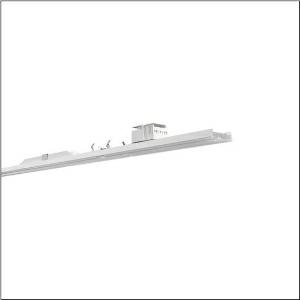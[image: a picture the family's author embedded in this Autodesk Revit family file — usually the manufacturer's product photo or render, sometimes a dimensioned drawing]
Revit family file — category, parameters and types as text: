
# Revit family: licross_r__11_recessed_mo_51tl18cn48xf_f7f9
name_source: partatom
category: Lighting Fixtures
units: mm (PartAtom-declared; Revit-internal decimal feet)

## family parameters
Cut with Voids When Loaded = No
Host = Face
Light Source = No
Part Type = Normal
Room Calculation Point = No
Round Connector Dimension = Use Diameter
Shared = No

## types (1)
- --- (1 x LED, 8060 lm, 48 W, 4000K)
    Apparent Load = 48 VA
    CIE Flux Codes = 83 96 99 100 100
    Color Rendering = 80
    Color Temperature = 4000K
    Default Elevation = 1800 mm
    Description = Licross® 11 Recessed MOluminaire insert, length: 1.500mm, width: 66mm, height: 67mm, LED rated luminous flux: 8.060lm, light colour: 840, control gear: ON/OFF Multilumen, CLOi, control gear: ECG Multilumen, with plug, 3-pole, with phase selection, mains connection: 220..240V, AC, 50/60Hz, halogen-free wiring, primary optical cover: cover, of PMMA, light emission: direct distribution, protection rating (complete): IP40, insulation class (complete): insulation class I (protective earthing), certification: CE, ENEC, VDE, protection symbol: D if used in an environment without relevant dust loads with corresponding accessories, permissible ambient temperature for indoor applications: -35..+40°C, reducing of maximum allowable ambient temperature of 5°C with ceiling mounting, corresponds to IFS (International Featured Standards) requirements for safety and quality in the food industry, packaging unit: 1 piece
    Height = 58 mm
    Lamp = 1 x LED
    Lamp Light Flux = 8060 lm
    Lamp Power = 48 W
    Lamp count = 1
    Length = 1500 mm
    Luminous efficacy = 168 lm/W
    Manufacturer = Siteco
    ModVariant = No
    Model = 51TL18CN48XF
    Mounting Place = Ceiling
    Mounting Type = Pendant
    Number of Poles = 1
    OnlyDefault = Yes
    Power Factor = 1
    Product Name = Licross® 11 Recessed MO
    Product group = luminaire insert
    ProductGroupID = 902
    Protection Class = Protection class I
    Protection Degree = IP 40
    RLX_Detail_Level = 1
    RlxData = <blob elided: 20065 chars, md5=a40b1835>
    Socket = socket
    Standby Power = 0 W
    System Light Flux = 8060 lm
    System Power = 48 W
    Type Comments = factory setting: luminous flux: 100 % | (A | C | E) | 109 mA
    Type Image = l_1266722.jpg
    URL = http://relux.com
    VarID = @adj_138657
    Voltage = 0 V
    Weight = 0.00 kg
    Width = 66 mm

## geometry (parser evidence)
native form markers: Blend x4, Sweep x11
no freeform markers — native parametric forms only
